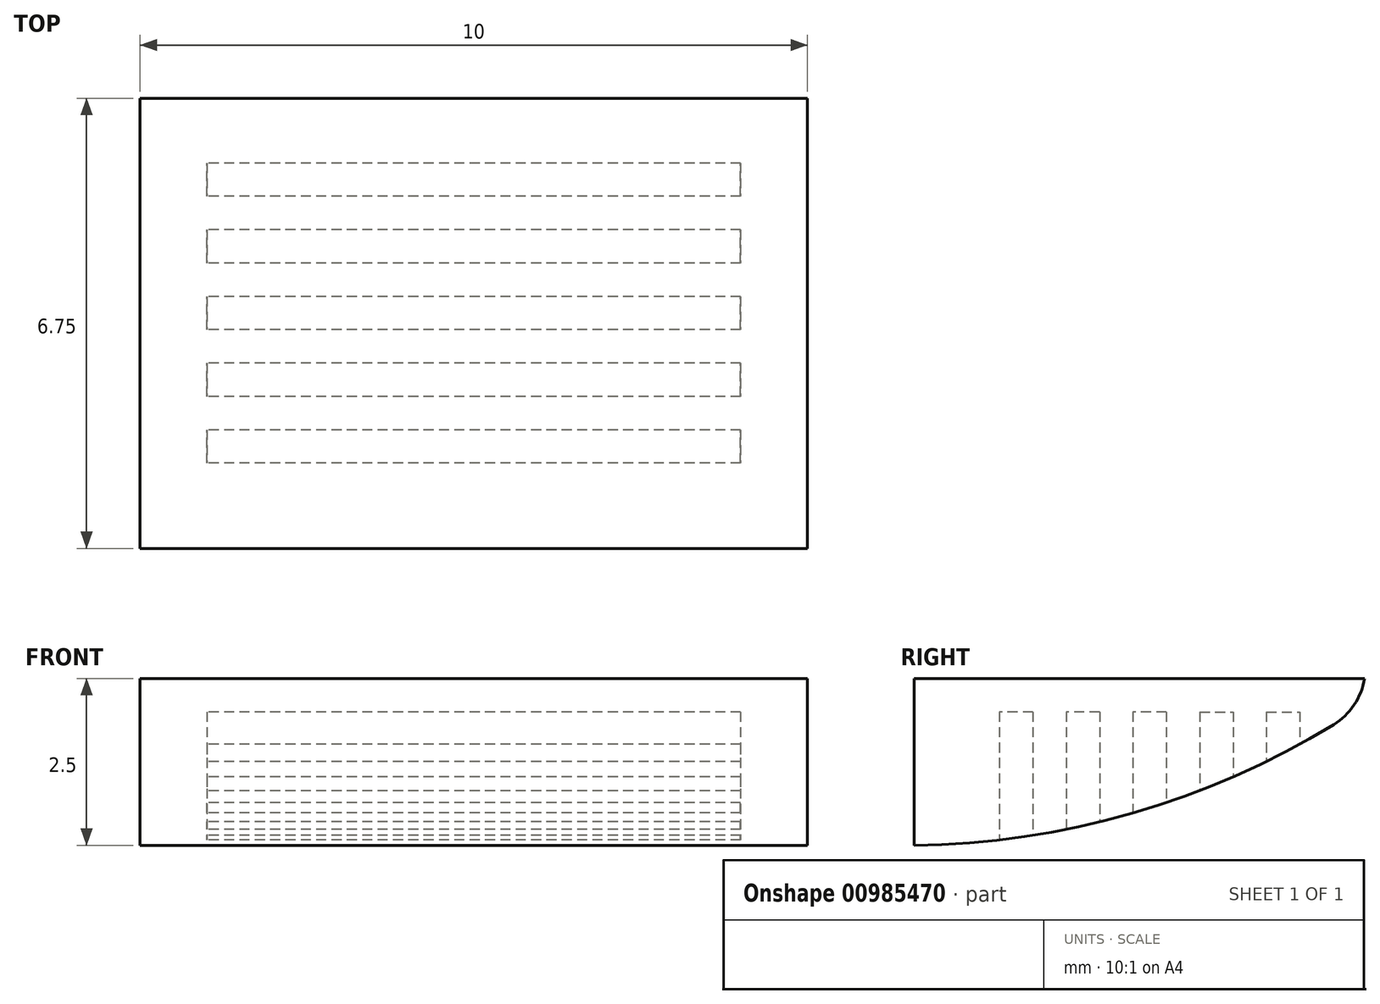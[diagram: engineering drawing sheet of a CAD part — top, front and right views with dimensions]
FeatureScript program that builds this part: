
annotation { "Feature Type Name" : "Feature", "Feature Type Description" : "" }
export const myFeature = defineFeature(function(context is Context, id is Id, definition is map)
    precondition{}
    {
        {
            var Q0;
            Q0=qCreatedBy(makeId("Top.planeOp"),FACE);
            var sketch = newSketch(context, id + "F0", { "sketchPlane" : qUnion([Q0])});
            skLineSegment(sketch, "E0.bottom", {"start": v(0, 0) * mm, "end": v(10, 0) * mm});
            skLineSegment(sketch, "E0.top", {"start": v(0, 7.14) * mm, "end": v(10, 7.14) * mm});
            skLineSegment(sketch, "E0.left", {"start": v(0, 0) * mm, "end": v(0, 7.14) * mm});
            skLineSegment(sketch, "E0.right", {"start": v(10, 0) * mm, "end": v(10, 7.14) * mm});
            skSolve(sketch);
        }
        {
            var Q0;
            Q0=qSketchRegion(id+"F0",true);
            extrude(context, id + "F1", {"entities" : qUnion([Q0]), "depth" : 2.5 * mm});
        }
        {
            var Q0;
            Q0=makeQuery(id+"F1.opExtrude","SWEPT_FACE",FACE,{"disambiguationData":[OSD([sQuery(id+"F0.wireOp",EDGE,"E0.left")])]});
            var sketch = newSketch(context, id + "F2", { "sketchPlane" : qUnion([Q0])});
            skLineSegment(sketch, "E1", {"start": v(0, 2.25) * mm, "end": v(0, 0) * mm});
            skArc(sketch, "E2", {"start": v(-6.75, 2.1) * mm, "mid": v(-3.53, 0.56) * mm, "end": v(0, 0) * mm});
            skLineSegment(sketch, "E3", {"start": v(-6.75, 2.1) * mm, "end": v(-6.75, 12.27) * mm});
            skLineSegment(sketch, "E4", {"start": v(-6.75, 12.27) * mm, "end": v(-9.83, -2.35) * mm});
            skLineSegment(sketch, "E5", {"start": v(-9.83, -2.35) * mm, "end": v(0, 0) * mm});
            skSolve(sketch);
        }
        {
            var Q0;
            Q0=qSketchRegion(id+"F2",true);
            extrude(context, id + "F3", {"entities" : qUnion([Q0]), "operationType" : NewBodyOperationType.REMOVE, "endBound" : BoundingType.THROUGH_ALL, "oppositeDirection" : true, "depth" : 25 * mm});
        }
        {
            var Q0;
            Q0=makeQuery(id+"F3.boolean.opBoolean","COPY",EDGE,{"derivedFrom":makeQuery(id+"F3.opExtrude","SWEPT_EDGE",EDGE,{"disambiguationData":[OSD([sQuery(id+"F2.wireOp",EDGE,"E2"),sQuery(id+"F2.wireOp",EDGE,"E3")])]})});
            fillet(context, id + "F4", {"entities" : qUnion([Q0]), "radius" : 1 * mm, "tangentPropagation" : true, "allowEdgeOverflow" : false});
        }
        {
            var Q0;
            Q0=makeQuery(id+"F1.opExtrude","CAP_FACE",FACE,{"disambiguationData":[OSD([sQuery(id+"F0.wireOp",EDGE,"E0.bottom"),sQuery(id+"F0.wireOp",EDGE,"E0.top"),sQuery(id+"F0.wireOp",EDGE,"E0.left"),sQuery(id+"F0.wireOp",EDGE,"E0.right")])],"isStart":false});
            cPlane(context, id + "F5", {"entities" : qUnion([Q0]), "cplaneType" : CPlaneType.OFFSET, "offset" : 2.5 * mm, "oppositeDirection" : true, "width" : 150 * mm, "height" : 150 * mm});
        }
        {
            var Q0;
            Q0=qCreatedBy(id+"F5.planeOp",FACE);
            var sketch = newSketch(context, id + "F6", { "sketchPlane" : qUnion([Q0])});
            skLineSegment(sketch, "E6.bottom", {"start": v(9, 4.28) * mm, "end": v(1, 4.28) * mm});
            skLineSegment(sketch, "E6.top", {"start": v(9, 3.78) * mm, "end": v(1, 3.78) * mm});
            skLineSegment(sketch, "E7.top", {"start": v(9, 3.28) * mm, "end": v(1, 3.28) * mm});
            skLineSegment(sketch, "E7.left", {"start": v(9, 3.78) * mm, "end": v(9, 3.28) * mm});
            skLineSegment(sketch, "E7.right", {"start": v(1, 3.78) * mm, "end": v(1, 3.28) * mm});
            skLineSegment(sketch, "E8.top", {"start": v(9, 2.78) * mm, "end": v(1, 2.78) * mm});
            skLineSegment(sketch, "E9.top", {"start": v(9, 2.28) * mm, "end": v(1, 2.28) * mm});
            skLineSegment(sketch, "E9.left", {"start": v(9, 2.78) * mm, "end": v(9, 2.28) * mm});
            skLineSegment(sketch, "E9.right", {"start": v(1, 2.78) * mm, "end": v(1, 2.28) * mm});
            skLineSegment(sketch, "E10.top", {"start": v(9, 1.78) * mm, "end": v(1, 1.78) * mm});
            skLineSegment(sketch, "E11.top", {"start": v(9, 1.28) * mm, "end": v(1, 1.28) * mm});
            skLineSegment(sketch, "E11.left", {"start": v(9, 1.78) * mm, "end": v(9, 1.28) * mm});
            skLineSegment(sketch, "E11.right", {"start": v(1, 1.78) * mm, "end": v(1, 1.28) * mm});
            skLineSegment(sketch, "E12.top", {"start": v(9, 4.78) * mm, "end": v(1, 4.78) * mm});
            skLineSegment(sketch, "E12.left", {"start": v(9, 4.28) * mm, "end": v(9, 4.78) * mm});
            skLineSegment(sketch, "E12.right", {"start": v(1, 4.28) * mm, "end": v(1, 4.78) * mm});
            skLineSegment(sketch, "E13.bottom", {"start": v(9, 5.28) * mm, "end": v(1, 5.28) * mm});
            skLineSegment(sketch, "E13.top", {"start": v(9, 5.78) * mm, "end": v(1, 5.78) * mm});
            skLineSegment(sketch, "E13.left", {"start": v(9, 5.28) * mm, "end": v(9, 5.78) * mm});
            skLineSegment(sketch, "E13.right", {"start": v(1, 5.28) * mm, "end": v(1, 5.78) * mm});
            skSolve(sketch);
        }
        {
            var Q0;
            Q0=qSketchRegion(id+"F6",true);
            extrude(context, id + "F7", {"entities" : qUnion([Q0]), "operationType" : NewBodyOperationType.REMOVE, "depth" : 2 * mm});
        }
    });
